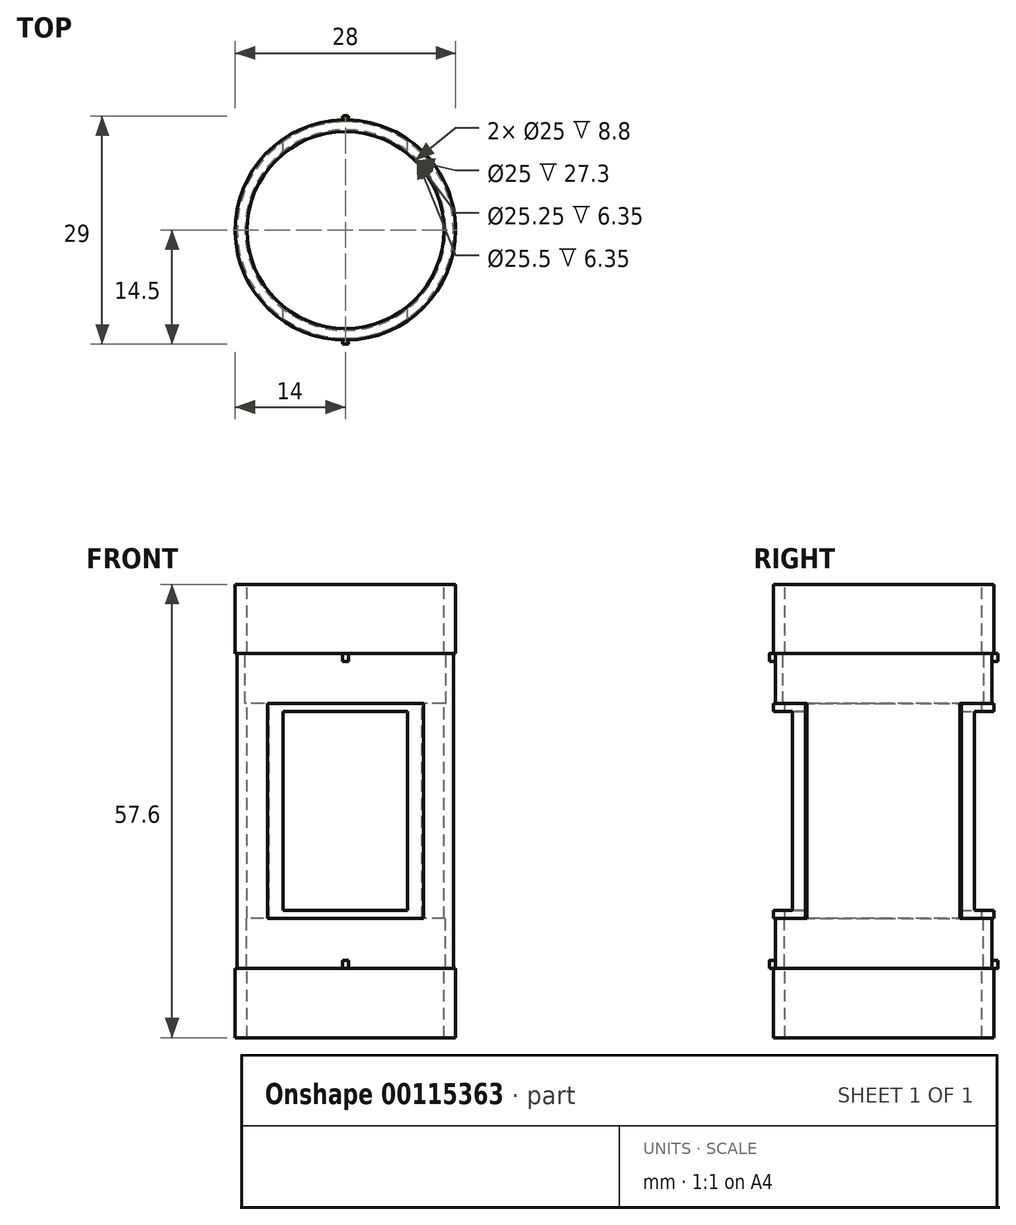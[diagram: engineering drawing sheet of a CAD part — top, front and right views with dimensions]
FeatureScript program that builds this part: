
annotation { "Feature Type Name" : "Feature", "Feature Type Description" : "" }
export const myFeature = defineFeature(function(context is Context, id is Id, definition is map)
    precondition{}
    {
        {
            var Q0;
            Q0=qCreatedBy(makeId("Top.planeOp"),FACE);
            var sketch = newSketch(context, id + "F0", { "sketchPlane" : qUnion([Q0])});
            skCircle(sketch, "E0", {"center": v(0, 0) * mm, "radius": 14 * mm});
            skSolve(sketch);
        }
        {
            var Q0;
            Q0 = qSketchRegion(id + "F0", true);
            extrude(context, id + "F1", {"entities" : qUnion([Q0]), "depth" : 57.6 * mm});
        }
        {
            var Q0;
            Q0=makeQuery(id+"F1.opExtrude","CAP_FACE",FACE,{"disambiguationData":[OSD([sQuery(id+"F0.wireOp",EDGE,"E0")])],"isStart":false});
            var sketch = newSketch(context, id + "F2", { "sketchPlane" : qUnion([Q0])});
            skCircle(sketch, "E1", {"center": v(0, 0) * mm, "radius": 12.5 * mm});
            skSolve(sketch);
        }
        {
            var Q0;
            Q0 = qSketchRegion(id + "F2", true);
            extrude(context, id + "F3", {"entities" : qUnion([Q0]), "operationType" : NewBodyOperationType.REMOVE, "endBound" : BoundingType.THROUGH_ALL, "oppositeDirection" : true, "depth" : 25 * mm});
        }
        {
            var Q0;
            Q0=qCreatedBy(makeId("Top.planeOp"),FACE);
            cPlane(context, id + "F4", {"entities" : qUnion([Q0]), "cplaneType" : CPlaneType.OFFSET, "offset" : ((57.6 - 40) / 2) * mm, "width" : 150 * mm, "height" : 150 * mm});
        }
        {
            var Q0;
            Q0=qCreatedBy(id+"F4.planeOp",FACE);
            var sketch = newSketch(context, id + "F5", { "sketchPlane" : qUnion([Q0])});
            skCircle(sketch, "E2", {"center": v(0, 0) * mm, "radius": 13.75 * mm});
            skCircle(sketch, "E3", {"center": v(0, 0) * mm, "radius": 20.07 * mm});
            skSolve(sketch);
        }
        {
            var Q0;
            Q0 = qSketchRegion(id + "F5", true);
            extrude(context, id + "F6", {"entities" : qUnion([Q0]), "operationType" : NewBodyOperationType.REMOVE, "depth" : 6.35 * mm});
        }
        {
            var Q0;
            Q0=qCreatedBy(id+"F4.planeOp",FACE);
            cPlane(context, id + "F7", {"entities" : qUnion([Q0]), "cplaneType" : CPlaneType.OFFSET, "offset" : 40 * mm, "width" : 150 * mm, "height" : 150 * mm});
        }
        {
            var Q0;
            Q0=qCreatedBy(id+"F7.planeOp",FACE);
            var sketch = newSketch(context, id + "F8", { "sketchPlane" : qUnion([Q0])});
            skCircle(sketch, "E4", {"center": v(0, 0) * mm, "radius": 13.75 * mm});
            skCircle(sketch, "E5", {"center": v(0, 0) * mm, "radius": 16.55 * mm});
            skSolve(sketch);
        }
        {
            var Q0;
            Q0 = qSketchRegion(id + "F8", true);
            extrude(context, id + "F9", {"entities" : qUnion([Q0]), "operationType" : NewBodyOperationType.REMOVE, "oppositeDirection" : true, "depth" : 6.35 * mm});
        }
        {
            var Q0;
            Q0=qCreatedBy(makeId("Front.planeOp"),FACE);
            var sketch = newSketch(context, id + "F10", { "sketchPlane" : qUnion([Q0])});
            skLineSegment(sketch, "E6.bottom", {"start": v(7.9, 16.15) * mm, "end": v(-7.9, 16.15) * mm});
            skLineSegment(sketch, "E6.top", {"start": v(7.9, 41.45) * mm, "end": v(-7.9, 41.45) * mm});
            skLineSegment(sketch, "E6.left", {"start": v(7.9, 16.15) * mm, "end": v(7.9, 41.45) * mm});
            skLineSegment(sketch, "E6.right", {"start": v(-7.9, 16.15) * mm, "end": v(-7.9, 41.45) * mm});
            skPoint(sketch, "E6.middle", {"position": v(0, 28.8) * mm});
            skSolve(sketch);
        }
        {
            var Q0;
            Q0 = qSketchRegion(id + "F10", true);
            extrude(context, id + "F11", {"entities" : qUnion([Q0]), "operationType" : NewBodyOperationType.REMOVE, "endBound" : BoundingType.THROUGH_ALL, "depth" : 25 * mm, "hasSecondDirection" : true, "secondDirectionOppositeDirection" : true, "secondDirectionDepth" : 25 * mm});
        }
        {
            var Q0;
            Q0=qCreatedBy(makeId("Front.planeOp"),FACE);
            var sketch = newSketch(context, id + "F12", { "sketchPlane" : qUnion([Q0])});
            skLineSegment(sketch, "E7.bottom", {"start": v(34.37, 8.8) * mm, "end": v(-34.37, 8.8) * mm});
            skLineSegment(sketch, "E7.top", {"start": v(34.37, 48.8) * mm, "end": v(-34.37, 48.8) * mm});
            skLineSegment(sketch, "E7.left", {"start": v(34.37, 8.8) * mm, "end": v(34.37, 48.8) * mm});
            skLineSegment(sketch, "E7.right", {"start": v(-34.37, 8.8) * mm, "end": v(-34.37, 48.8) * mm});
            skPoint(sketch, "E7.middle", {"position": v(0, 28.8) * mm});
            skLineSegment(sketch, "E8.bottom", {"start": v(13.75, 8.8) * mm, "end": v(-13.75, 8.8) * mm});
            skLineSegment(sketch, "E8.top", {"start": v(13.75, 48.8) * mm, "end": v(-13.75, 48.8) * mm});
            skLineSegment(sketch, "E8.left", {"start": v(13.75, 8.8) * mm, "end": v(13.75, 48.8) * mm});
            skLineSegment(sketch, "E8.right", {"start": v(-13.75, 8.8) * mm, "end": v(-13.75, 48.8) * mm});
            skSolve(sketch);
        }
        {
            var Q0;
            {var subQ0=sQuery(id+"F12.wireOp",EDGE,"E7.left");Q0=makeQuery(id+"F12.imprint","IMPRINT",FACE,{"disambiguationData":[TD([[makeQuery(id+"F12.imprint","IMPRINT",EDGE,{"derivedFrom":subQ0}),1.0]])]});}
            var Q1;
            {var subQ0=sQuery(id+"F12.wireOp",EDGE,"E7.right");Q1=makeQuery(id+"F12.imprint","IMPRINT",FACE,{"disambiguationData":[TD([[makeQuery(id+"F12.imprint","IMPRINT",EDGE,{"derivedFrom":subQ0}),-1.0]])]});}
            var Q2;
            {var subQ0=makeQuery(id+"F6.opExtrude","CAP_FACE",FACE,{"disambiguationData":[OSD([sQuery(id+"F5.wireOp",EDGE,"E2"),sQuery(id+"F5.wireOp",EDGE,"E3")])],"isStart":false});var subQ1=sQuery(id+"F0.wireOp",EDGE,"E0");Q2=makeQuery(id+"F9.boolean.opBoolean","SPLIT",FACE,{"disambiguationData":[TD([makeQuery(id+"F6.boolean.opBoolean","COPY",FACE,{"derivedFrom":subQ0})])],"derivedFrom":makeQuery(id+"F6.boolean.opBoolean","SPLIT",FACE,{"disambiguationData":[TD([makeQuery(id+"F1.opExtrude","CAP_FACE",FACE,{"disambiguationData":[OSD([subQ1])],"isStart":false})])],"derivedFrom":makeQuery(id+"F1.opExtrude","SWEPT_FACE",FACE,{"disambiguationData":[OSD([subQ1])]})})});}
            revolve(context, id + "F13", {"operationType" : NewBodyOperationType.REMOVE, "entities" : qUnion([Q0, Q1]), "axis" : qUnion([Q2]), "revolveType" : RevolveType.TWO_DIRECTIONS, "oppositeDirection" : true, "angle" : 45 * degree, "angleBack" : 315 * degree});
        }
        {
            var Q0;
            Q0=qCreatedBy(id+"F4.planeOp",FACE);
            var sketch = newSketch(context, id + "F14", { "sketchPlane" : qUnion([Q0])});
            skCircle(sketch, "E9", {"center": v(0, 0) * mm, "radius": 12.62 * mm});
            skSolve(sketch);
        }
        {
            var Q0;
            Q0 = qSketchRegion(id + "F14", true);
            extrude(context, id + "F15", {"entities" : qUnion([Q0]), "operationType" : NewBodyOperationType.REMOVE, "depth" : 6.35 * mm});
        }
        {
            var Q0;
            Q0=qCreatedBy(id+"F7.planeOp",FACE);
            var sketch = newSketch(context, id + "F16", { "sketchPlane" : qUnion([Q0])});
            skCircle(sketch, "E10", {"center": v(0, 0) * mm, "radius": 12.75 * mm});
            skSolve(sketch);
        }
        {
            var Q0;
            Q0 = qSketchRegion(id + "F16", true);
            extrude(context, id + "F17", {"entities" : qUnion([Q0]), "operationType" : NewBodyOperationType.REMOVE, "oppositeDirection" : true, "depth" : 6.35 * mm});
        }
        {
            var Q0;
            Q0=qCreatedBy(makeId("Right.planeOp"),FACE);
            var sketch = newSketch(context, id + "F18", { "sketchPlane" : qUnion([Q0])});
            skLineSegment(sketch, "E11.bottom", {"start": v(14.5, 8.8) * mm, "end": v(-14.5, 8.8) * mm});
            skLineSegment(sketch, "E11.top", {"start": v(14.5, 48.8) * mm, "end": v(-14.5, 48.8) * mm});
            skLineSegment(sketch, "E11.left", {"start": v(14.5, 8.8) * mm, "end": v(14.5, 48.8) * mm});
            skLineSegment(sketch, "E11.right", {"start": v(-14.5, 8.8) * mm, "end": v(-14.5, 48.8) * mm});
            skPoint(sketch, "E11.middle", {"position": v(0, 28.8) * mm});
            skLineSegment(sketch, "E12.bottom", {"start": v(14.5, 9.8) * mm, "end": v(-14.5, 9.8) * mm});
            skLineSegment(sketch, "E12.top", {"start": v(14.5, 47.8) * mm, "end": v(-14.5, 47.8) * mm});
            skLineSegment(sketch, "E12.left", {"start": v(14.5, 9.8) * mm, "end": v(14.5, 47.8) * mm});
            skLineSegment(sketch, "E12.right", {"start": v(-14.5, 9.8) * mm, "end": v(-14.5, 47.8) * mm});
            skLineSegment(sketch, "E13.bottom", {"start": v(13.75, 8.8) * mm, "end": v(-13.75, 8.8) * mm});
            skLineSegment(sketch, "E13.top", {"start": v(13.75, 48.8) * mm, "end": v(-13.75, 48.8) * mm});
            skLineSegment(sketch, "E13.left", {"start": v(13.75, 8.8) * mm, "end": v(13.75, 48.8) * mm});
            skLineSegment(sketch, "E13.right", {"start": v(-13.75, 8.8) * mm, "end": v(-13.75, 48.8) * mm});
            skSolve(sketch);
        }
        {
            var Q0;
            {var subQ0=sQuery(id+"F18.wireOp",EDGE,"E11.right");var subQ1=sQuery(id+"F18.wireOp",EDGE,"E11.top");var subQ2=makeQuery(id+"F18.imprint","INTERSECT",VERTEX,{"derivedFrom":[subQ1,subQ0]});Q0=makeQuery(id+"F18.imprint","IMPRINT",FACE,{"disambiguationData":[TD([[makeQuery(id+"F18.imprint","IMPRINT",EDGE,{"disambiguationData":[TD([[subQ2,1.0]])],"derivedFrom":subQ1}),1.0]])]});}
            var Q1;
            {var subQ0=sQuery(id+"F18.wireOp",EDGE,"E11.left");var subQ1=sQuery(id+"F18.wireOp",EDGE,"E11.top");var subQ2=makeQuery(id+"F18.imprint","INTERSECT",VERTEX,{"derivedFrom":[subQ1,subQ0]});Q1=makeQuery(id+"F18.imprint","IMPRINT",FACE,{"disambiguationData":[TD([[makeQuery(id+"F18.imprint","IMPRINT",EDGE,{"disambiguationData":[TD([[subQ2,-1.0]])],"derivedFrom":subQ1}),1.0]])]});}
            var Q2;
            {var subQ0=sQuery(id+"F18.wireOp",EDGE,"E11.left");var subQ1=sQuery(id+"F18.wireOp",EDGE,"E11.bottom");var subQ2=makeQuery(id+"F18.imprint","INTERSECT",VERTEX,{"derivedFrom":[subQ1,subQ0]});Q2=makeQuery(id+"F18.imprint","IMPRINT",FACE,{"disambiguationData":[TD([[makeQuery(id+"F18.imprint","IMPRINT",EDGE,{"disambiguationData":[TD([[subQ2,-1.0]])],"derivedFrom":subQ1}),-1.0]])]});}
            var Q3;
            {var subQ0=sQuery(id+"F18.wireOp",EDGE,"E11.right");var subQ1=sQuery(id+"F18.wireOp",EDGE,"E11.bottom");var subQ2=makeQuery(id+"F18.imprint","INTERSECT",VERTEX,{"derivedFrom":[subQ1,subQ0]});Q3=makeQuery(id+"F18.imprint","IMPRINT",FACE,{"disambiguationData":[TD([[makeQuery(id+"F18.imprint","IMPRINT",EDGE,{"disambiguationData":[TD([[subQ2,1.0]])],"derivedFrom":subQ1}),-1.0]])]});}
            var Q4;
            Q4=makeQuery(id+"F13.boolean.opBoolean","MERGE",FACE,{"derivedFrom":[makeQuery(id+"F6.boolean.opBoolean","COPY",FACE,{"derivedFrom":makeQuery(id+"F6.opExtrude","SWEPT_FACE",FACE,{"disambiguationData":[OSD([sQuery(id+"F5.wireOp",EDGE,"E2")])]})}),makeQuery(id+"F9.boolean.opBoolean","COPY",FACE,{"derivedFrom":makeQuery(id+"F9.opExtrude","SWEPT_FACE",FACE,{"disambiguationData":[OSD([sQuery(id+"F8.wireOp",EDGE,"E4")])]})}),makeQuery(id+"F13.opRevolve","SWEPT_FACE",FACE,{"disambiguationData":[OSD([sQuery(id+"F12.wireOp",EDGE,"E8.left")])]}),makeQuery(id+"F13.opRevolve","SWEPT_FACE",FACE,{"disambiguationData":[OSD([sQuery(id+"F12.wireOp",EDGE,"E8.right")])]})]});
            revolve(context, id + "F19", {"operationType" : NewBodyOperationType.ADD, "entities" : qUnion([Q0, Q1, Q2, Q3]), "axis" : qUnion([Q4]), "revolveType" : RevolveType.SYMMETRIC, "angle" : 3 * degree});
        }
    });
